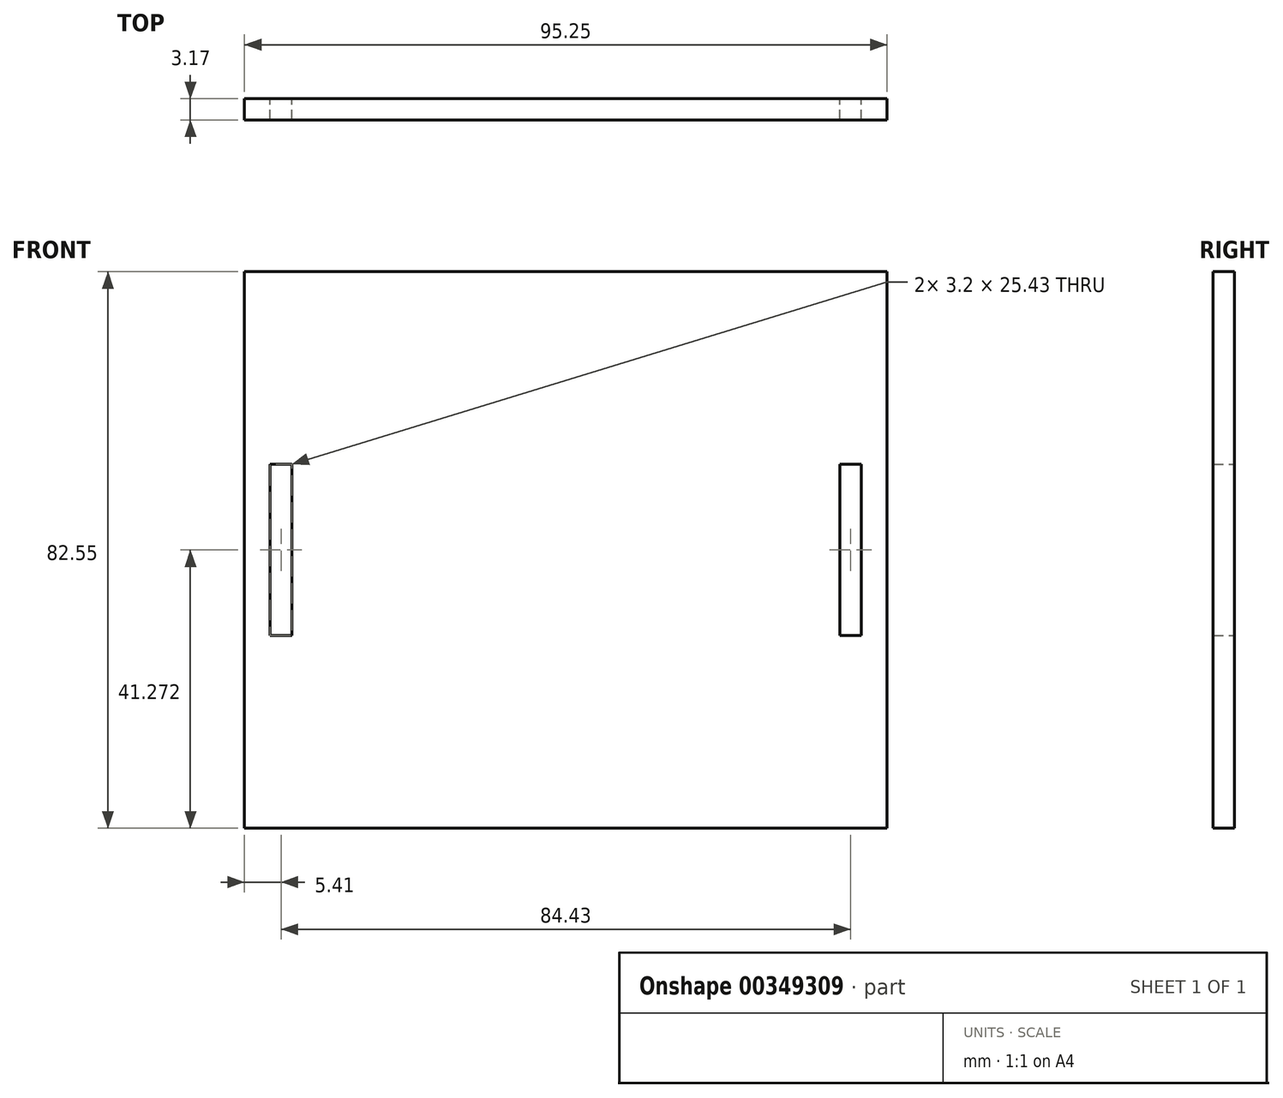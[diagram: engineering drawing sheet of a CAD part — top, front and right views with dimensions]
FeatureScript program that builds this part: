
annotation { "Feature Type Name" : "Feature", "Feature Type Description" : "" }
export const myFeature = defineFeature(function(context is Context, id is Id, definition is map)
    precondition{}
    {
        {
            var Q0;
            Q0=qCreatedBy(makeId("Front.planeOp"),FACE);
            var sketch = newSketch(context, id + "F0", { "sketchPlane" : qUnion([Q0])});
            skLineSegment(sketch, "E0.bottom", {"start": v(-95.23, 34.8) * mm, "end": v(0.02, 34.8) * mm});
            skLineSegment(sketch, "E0.top", {"start": v(-95.23, -47.74) * mm, "end": v(0.02, -47.74) * mm});
            skLineSegment(sketch, "E0.left", {"start": v(-95.23, 34.8) * mm, "end": v(-95.23, -47.74) * mm});
            skLineSegment(sketch, "E0.right", {"start": v(0.02, 34.8) * mm, "end": v(0.02, -47.74) * mm});
            skLineSegment(sketch, "E1.bottom", {"start": v(-91.42, 6.24) * mm, "end": v(-88.22, 6.24) * mm});
            skLineSegment(sketch, "E1.top", {"start": v(-91.42, -19.18) * mm, "end": v(-88.22, -19.18) * mm});
            skLineSegment(sketch, "E1.left", {"start": v(-91.42, 6.24) * mm, "end": v(-91.42, -19.18) * mm});
            skLineSegment(sketch, "E1.right", {"start": v(-88.22, 6.24) * mm, "end": v(-88.22, -19.18) * mm});
            skPoint(sketch, "E2", {"position": v(-88.22, -6.47) * mm});
            skPoint(sketch, "E3", {"position": v(-95.23, -6.47) * mm});
            skPoint(sketch, "E4", {"position": v(0.02, -6.47) * mm});
            skLineSegment(sketch, "E5.bottom", {"start": v(-7, 6.24) * mm, "end": v(-3.8, 6.24) * mm});
            skLineSegment(sketch, "E5.top", {"start": v(-7, -19.18) * mm, "end": v(-3.8, -19.18) * mm});
            skLineSegment(sketch, "E5.left", {"start": v(-7, 6.24) * mm, "end": v(-7, -19.18) * mm});
            skLineSegment(sketch, "E5.right", {"start": v(-3.8, 6.24) * mm, "end": v(-3.8, -19.18) * mm});
            skPoint(sketch, "E6", {"position": v(-7, -6.47) * mm});
            skLineSegment(sketch, "E7.bottom", {"start": v(-80.43, 34.8) * mm, "end": v(-55, 34.8) * mm});
            skLineSegment(sketch, "E7.top", {"start": v(-80.43, 37.98) * mm, "end": v(-55, 37.98) * mm});
            skLineSegment(sketch, "E7.left", {"start": v(-80.43, 34.8) * mm, "end": v(-80.43, 37.98) * mm});
            skLineSegment(sketch, "E7.right", {"start": v(-55, 34.8) * mm, "end": v(-55, 37.98) * mm});
            skLineSegment(sketch, "E8.bottom", {"start": v(-40.2, 34.8) * mm, "end": v(-14.78, 34.8) * mm});
            skLineSegment(sketch, "E8.top", {"start": v(-40.2, 37.98) * mm, "end": v(-14.78, 37.98) * mm});
            skLineSegment(sketch, "E8.left", {"start": v(-40.2, 34.8) * mm, "end": v(-40.2, 37.98) * mm});
            skLineSegment(sketch, "E8.right", {"start": v(-14.78, 34.8) * mm, "end": v(-14.78, 37.98) * mm});
            skLineSegment(sketch, "E9.bottom", {"start": v(-80.43, -47.74) * mm, "end": v(-55, -47.74) * mm});
            skLineSegment(sketch, "E9.top", {"start": v(-80.43, -50.92) * mm, "end": v(-55, -50.92) * mm});
            skLineSegment(sketch, "E9.left", {"start": v(-80.43, -47.74) * mm, "end": v(-80.43, -50.92) * mm});
            skLineSegment(sketch, "E9.right", {"start": v(-55, -47.74) * mm, "end": v(-55, -50.92) * mm});
            skLineSegment(sketch, "E10.bottom", {"start": v(-40.2, -47.74) * mm, "end": v(-14.78, -47.74) * mm});
            skLineSegment(sketch, "E10.top", {"start": v(-40.2, -50.92) * mm, "end": v(-14.78, -50.92) * mm});
            skLineSegment(sketch, "E10.left", {"start": v(-40.2, -47.74) * mm, "end": v(-40.2, -50.92) * mm});
            skLineSegment(sketch, "E10.right", {"start": v(-14.78, -47.74) * mm, "end": v(-14.78, -50.92) * mm});
            skSolve(sketch);
        }
        {
            var Q0;
            Q0=makeQuery(id+"F0.imprint","IMPRINT",FACE,{"disambiguationData":[TD([[makeQuery(id+"F0.imprint","IMPRINT",EDGE,{"derivedFrom":sQuery(id+"F0.wireOp",EDGE,"E0.bottom")}),-1.0]])]});
            var Q1;
            Q1=makeQuery(id+"F0.imprint","IMPRINT",FACE,{"disambiguationData":[TD([[makeQuery(id+"F0.imprint","IMPRINT",EDGE,{"derivedFrom":sQuery(id+"F0.wireOp",EDGE,"E7.bottom")}),1.0]])]});
            var Q2;
            Q2=makeQuery(id+"F0.imprint","IMPRINT",FACE,{"disambiguationData":[TD([[makeQuery(id+"F0.imprint","IMPRINT",EDGE,{"derivedFrom":sQuery(id+"F0.wireOp",EDGE,"E8.bottom")}),1.0]])]});
            var Q3;
            Q3=makeQuery(id+"F0.imprint","IMPRINT",FACE,{"disambiguationData":[TD([[makeQuery(id+"F0.imprint","IMPRINT",EDGE,{"derivedFrom":sQuery(id+"F0.wireOp",EDGE,"E10.bottom")}),-1.0]])]});
            var Q4;
            Q4=makeQuery(id+"F0.imprint","IMPRINT",FACE,{"disambiguationData":[TD([[makeQuery(id+"F0.imprint","IMPRINT",EDGE,{"derivedFrom":sQuery(id+"F0.wireOp",EDGE,"E9.bottom")}),-1.0]])]});
            extrude(context, id + "F1", {"entities" : qUnion([Q0, Q1, Q2, Q3, Q4]), "depth" : 3.17 * mm});
        }
    });
